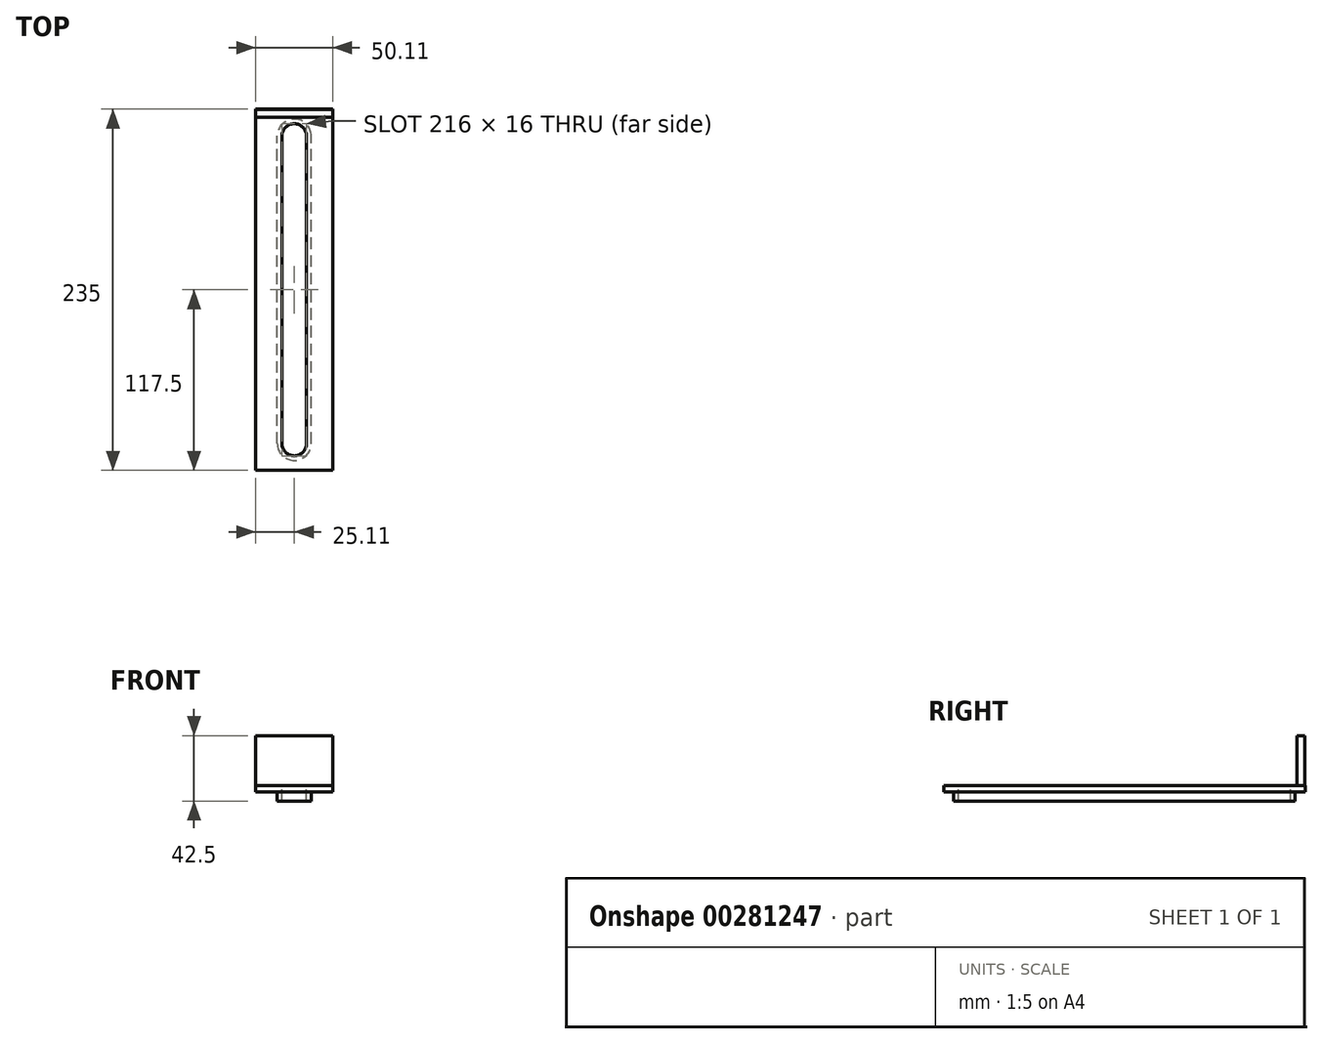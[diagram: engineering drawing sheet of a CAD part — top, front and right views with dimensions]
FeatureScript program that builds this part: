
annotation { "Feature Type Name" : "Feature", "Feature Type Description" : "" }
export const myFeature = defineFeature(function(context is Context, id is Id, definition is map)
    precondition{}
    {
        {
            var Q0;
            Q0=qCreatedBy(makeId("Top.planeOp"),FACE);
            var sketch = newSketch(context, id + "F0", { "sketchPlane" : qUnion([Q0])});
            skLineSegment(sketch, "E0.bottom", {"start": v(25, -117.5) * mm, "end": v(-25, -117.5) * mm});
            skLineSegment(sketch, "E0.top", {"start": v(25, 117.5) * mm, "end": v(-25, 117.5) * mm});
            skLineSegment(sketch, "E0.left", {"start": v(25, -117.5) * mm, "end": v(25, 117.5) * mm});
            skLineSegment(sketch, "E0.right", {"start": v(-25, -117.5) * mm, "end": v(-25, 117.5) * mm});
            skPoint(sketch, "E0.middle", {"position": v(0, 0) * mm});
            skLineSegment(sketch, "E1.left", {"start": v(8, -100) * mm, "end": v(8, 100) * mm});
            skLineSegment(sketch, "E1.right", {"start": v(-8, -100) * mm, "end": v(-8, 100) * mm});
            skArc(sketch, "E2", {"start": v(-8, -100) * mm, "mid": v(0, -108) * mm, "end": v(8, -100) * mm});
            skArc(sketch, "E3", {"start": v(8, 100) * mm, "mid": v(0, 108) * mm, "end": v(-8, 100) * mm});
            skLineSegment(sketch, "E4.left", {"start": v(11, -100) * mm, "end": v(11, 100) * mm});
            skLineSegment(sketch, "E4.right", {"start": v(-11, -100) * mm, "end": v(-11, 100) * mm});
            skArc(sketch, "E5", {"start": v(-11, -100) * mm, "mid": v(0, -111) * mm, "end": v(11, -100) * mm});
            skArc(sketch, "E6", {"start": v(11, 100) * mm, "mid": v(0, 111) * mm, "end": v(-11, 100) * mm});
            skSolve(sketch);
        }
        {
            var Q0;
            Q0=qSketchRegion(id+"F0",true);
            extrude(context, id + "F1", {"entities" : qUnion([Q0]), "depth" : 4 * mm});
        }
        {
            var Q0;
            Q0=makeQuery(id+"F0.imprint","IMPRINT",FACE,{"disambiguationData":[TD([[makeQuery(id+"F0.imprint","IMPRINT",EDGE,{"derivedFrom":sQuery(id+"F0.wireOp",EDGE,"E1.left")}),-1.0]])]});
            extrude(context, id + "F2", {"entities" : qUnion([Q0]), "operationType" : NewBodyOperationType.ADD, "depth" : 10 * mm});
        }
        {
            var Q0;
            Q0=makeQuery(id+"F1.opExtrude","SWEPT_BODY",BODY,{"disambiguationData":[OSD([sQuery(id+"F0.wireOp",EDGE,"E0.bottom"),sQuery(id+"F0.wireOp",EDGE,"E0.top"),sQuery(id+"F0.wireOp",EDGE,"E0.left"),sQuery(id+"F0.wireOp",EDGE,"E0.right"),sQuery(id+"F0.wireOp",EDGE,"E4.left"),sQuery(id+"F0.wireOp",EDGE,"E4.right"),sQuery(id+"F0.wireOp",EDGE,"E5"),sQuery(id+"F0.wireOp",EDGE,"E6")])]});
            var Q1;
            Q1=sQuery(id+"F0.wireOp",EDGE,"E1.right");
            transform(context, id + "F3", {"entities" : qUnion([Q0]), "transformType" : TransformType.ROTATION, "transformAxis" : qUnion([Q1]), "angle" : 180 * degree, "makeCopy" : false});
        }
        {
            var Q0;
            Q0=makeQuery(id+"F1.opExtrude","SWEPT_BODY",BODY,{"disambiguationData":[OSD([sQuery(id+"F0.wireOp",EDGE,"E0.bottom"),sQuery(id+"F0.wireOp",EDGE,"E0.top"),sQuery(id+"F0.wireOp",EDGE,"E0.left"),sQuery(id+"F0.wireOp",EDGE,"E0.right"),sQuery(id+"F0.wireOp",EDGE,"E4.left"),sQuery(id+"F0.wireOp",EDGE,"E4.right"),sQuery(id+"F0.wireOp",EDGE,"E5"),sQuery(id+"F0.wireOp",EDGE,"E6")])]});
            transform(context, id + "F4", {"entities" : qUnion([Q0]), "transformType" : TransformType.TRANSLATION_3D, "dx" : 16 * mm, "dy" : 0 * mm, "dz" : 0 * mm, "makeCopy" : false});
        }
        {
            var Q0;
            Q0=makeQuery(id+"F0.imprint","IMPRINT",FACE,{"disambiguationData":[TD([[makeQuery(id+"F0.imprint","IMPRINT",EDGE,{"derivedFrom":sQuery(id+"F0.wireOp",EDGE,"E0.bottom")}),-1.0]])]});
            var sketch = newSketch(context, id + "F5", { "sketchPlane" : qUnion([Q0])});
            skLineSegment(sketch, "E7.bottom", {"start": v(-25.1, 117.3) * mm, "end": v(24.9, 117.3) * mm});
            skLineSegment(sketch, "E7.top", {"start": v(-25.1, 112.3) * mm, "end": v(24.9, 112.3) * mm});
            skLineSegment(sketch, "E7.left", {"start": v(-25.1, 117.3) * mm, "end": v(-25.1, 112.3) * mm});
            skLineSegment(sketch, "E7.right", {"start": v(24.9, 117.3) * mm, "end": v(24.9, 112.3) * mm});
            skSolve(sketch);
        }
        {
            var Q0;
            Q0=qSketchRegion(id+"F5",true);
            extrude(context, id + "F6", {"entities" : qUnion([Q0]), "operationType" : NewBodyOperationType.ADD, "depth" : 32.5 * mm});
        }
    });
